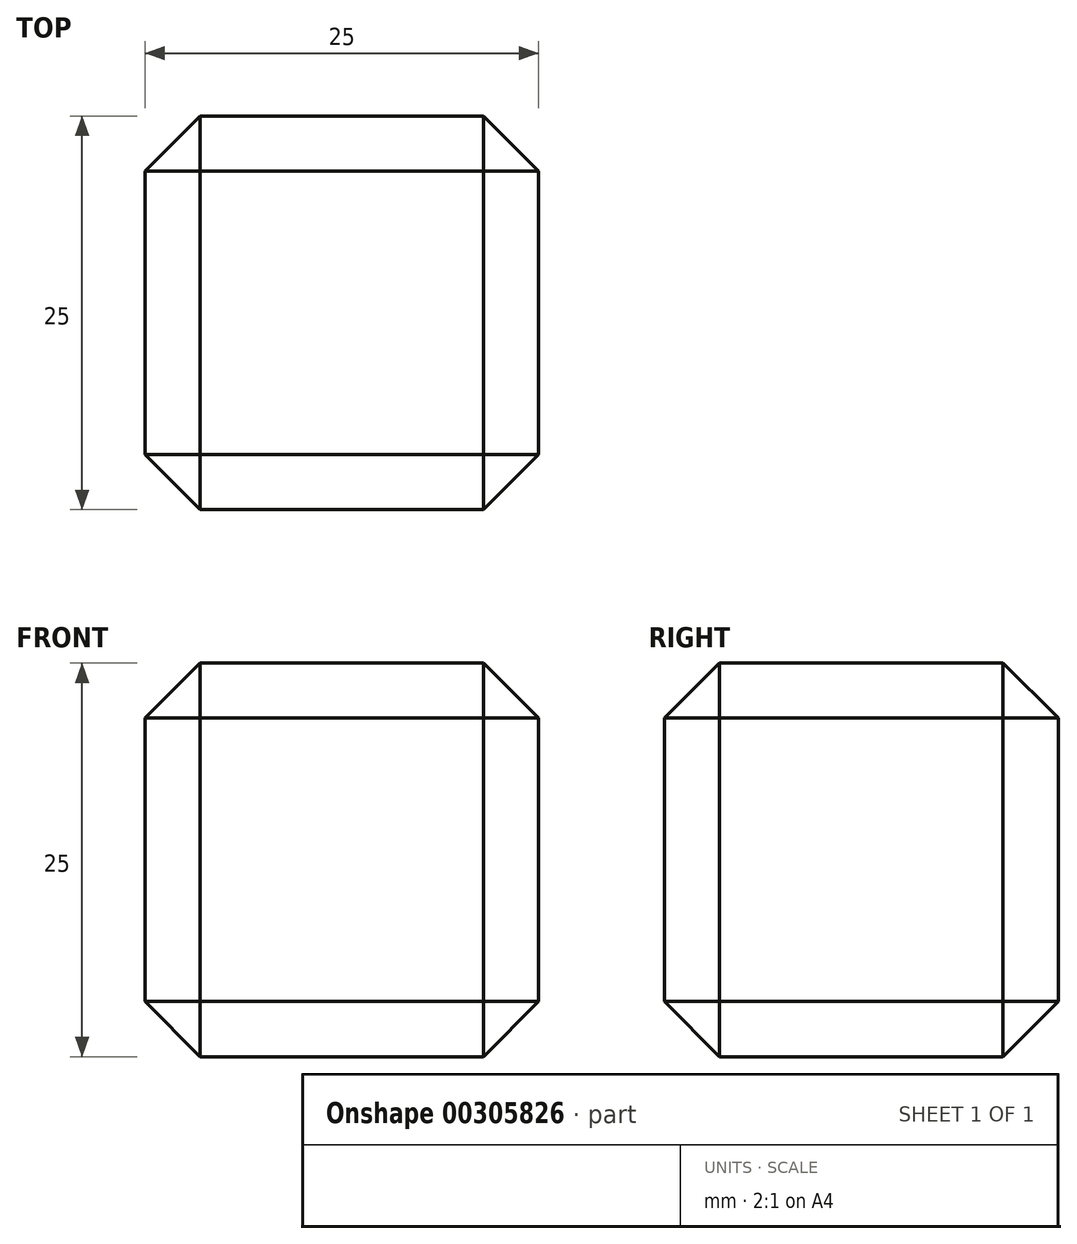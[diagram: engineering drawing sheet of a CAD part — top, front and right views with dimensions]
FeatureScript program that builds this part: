
annotation { "Feature Type Name" : "Feature", "Feature Type Description" : "" }
export const myFeature = defineFeature(function(context is Context, id is Id, definition is map)
    precondition{}
    {
        {
            var Q0;
            Q0=qCreatedBy(makeId("Top.planeOp"),FACE);
            var sketch = newSketch(context, id + "F0", { "sketchPlane" : qUnion([Q0])});
            skLineSegment(sketch, "E0.bottom", {"start": v(12.5, 12.5) * mm, "end": v(-12.5, 12.5) * mm});
            skLineSegment(sketch, "E0.top", {"start": v(12.5, -12.5) * mm, "end": v(-12.5, -12.5) * mm});
            skLineSegment(sketch, "E0.left", {"start": v(12.5, 12.5) * mm, "end": v(12.5, -12.5) * mm});
            skLineSegment(sketch, "E0.right", {"start": v(-12.5, 12.5) * mm, "end": v(-12.5, -12.5) * mm});
            skPoint(sketch, "E0.middle", {"position": v(0, 0) * mm});
            skSolve(sketch);
        }
        {
            var Q0;
            Q0=makeQuery(id+"F0.imprint","IMPRINT",FACE,{"disambiguationData":[TD([[makeQuery(id+"F0.imprint","IMPRINT",EDGE,{"derivedFrom":sQuery(id+"F0.wireOp",EDGE,"E0.bottom")}),1.0]])]});
            extrude(context, id + "F1", {"entities" : qUnion([Q0]), "endBound" : BoundingType.SYMMETRIC, "depth" : 25 * mm});
        }
        {
            var Q0;
            Q0=makeQuery(id+"F1.opExtrude","SWEPT_FACE",FACE,{"disambiguationData":[OSD([sQuery(id+"F0.wireOp",EDGE,"E0.top")])]});
            var Q1;
            Q1=makeQuery(id+"F1.opExtrude","CAP_FACE",FACE,{"disambiguationData":[OSD([sQuery(id+"F0.wireOp",EDGE,"E0.bottom"),sQuery(id+"F0.wireOp",EDGE,"E0.top"),sQuery(id+"F0.wireOp",EDGE,"E0.left"),sQuery(id+"F0.wireOp",EDGE,"E0.right")])],"isStart":false});
            var Q2;
            Q2=makeQuery(id+"F1.opExtrude","SWEPT_FACE",FACE,{"disambiguationData":[OSD([sQuery(id+"F0.wireOp",EDGE,"E0.right")])]});
            var Q3;
            Q3=makeQuery(id+"F1.opExtrude","SWEPT_FACE",FACE,{"disambiguationData":[OSD([sQuery(id+"F0.wireOp",EDGE,"E0.left")])]});
            var Q4;
            Q4=makeQuery(id+"F1.opExtrude","SWEPT_FACE",FACE,{"disambiguationData":[OSD([sQuery(id+"F0.wireOp",EDGE,"E0.bottom")])]});
            var Q5;
            Q5=makeQuery(id+"F1.opExtrude","CAP_FACE",FACE,{"disambiguationData":[OSD([sQuery(id+"F0.wireOp",EDGE,"E0.bottom"),sQuery(id+"F0.wireOp",EDGE,"E0.top"),sQuery(id+"F0.wireOp",EDGE,"E0.left"),sQuery(id+"F0.wireOp",EDGE,"E0.right")])],"isStart":true});
            chamfer(context, id + "F2", {"entities" : qUnion([Q0, Q1, Q2, Q3, Q4, Q5]), "width" : 3.5 * mm, "tangentPropagation" : true});
        }
    });
